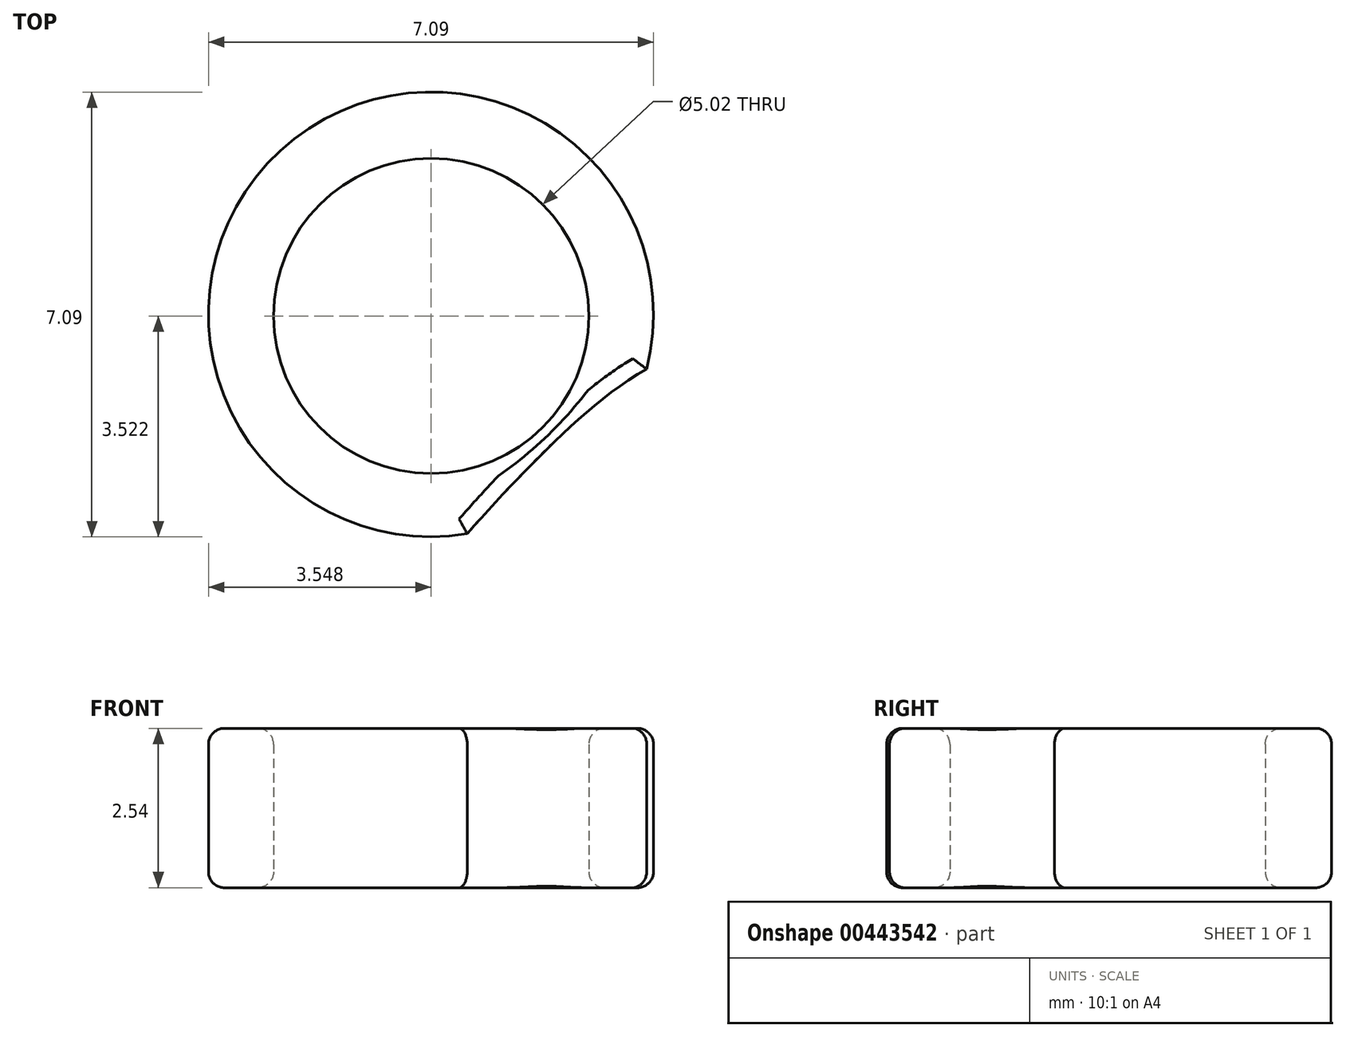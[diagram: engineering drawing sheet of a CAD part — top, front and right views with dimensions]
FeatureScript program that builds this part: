
annotation { "Feature Type Name" : "Feature", "Feature Type Description" : "" }
export const myFeature = defineFeature(function(context is Context, id is Id, definition is map)
    precondition{}
    {
        {
            var Q0;
            Q0=qCreatedBy(makeId("Top.planeOp"),FACE);
            var sketch = newSketch(context, id + "F0", { "sketchPlane" : qUnion([Q0])});
            skPoint(sketch, "E0.middle", {"position": v(0, 0) * mm});
            skFitSpline(sketch, "E1", {"points": [v(4.9, 17.87) * mm, v(1.19, 13.9) * mm, v(-0.75, 10.51) * mm, v(-1.88, 7.28) * mm, v(-2.45, 4.3) * mm, v(-2.45, 2.67) * mm, v(-2.45, 1.7) * mm, v(-2.53, 1.67) * mm, v(-2.84, 1.9) * mm, v(-3.8, 2.6) * mm, v(-6.06, 3.65) * mm, v(-8.48, 4.46) * mm, v(-10.99, 4.94) * mm, v(-12.12, 5.02) * mm, v(-12.52, 5.19) * mm, v(-13.9, 5.83) * mm, v(-15.51, 6.72) * mm, v(-17.05, 7.45) * mm, v(-17.7, 7.7) * mm, v(-18.2, 7.68) * mm, v(-18.43, 7.5) * mm, v(-18.4, 7.12) * mm, v(-18.06, 6.75) * mm, v(-17.5, 6.42) * mm, v(-15.46, 4.52) * mm, v(-13.92, 2.7) * mm, v(-12.57, 0.87) * mm, v(-11.56, -0.71) * mm, v(-10.31, -2.54) * mm, v(-8.68, -4.65) * mm, v(-7.29, -6.28) * mm, v(-5.5, -7.74) * mm, v(-4.25, -8.58) * mm, v(-3.82, -8.8) * mm, v(-3.8, -8.88) * mm, v(-3.94, -8.97) * mm, v(-4.5, -9.48) * mm, v(-5.62, -10.4) * mm, v(-6.9, -11.54) * mm, v(-8.08, -12.6) * mm, v(-9.05, -13.45) * mm, v(-10.59, -15) * mm, v(-12.5, -16.77) * mm, v(-13.39, -17.72) * mm, v(-14.07, -18.53) * mm, v(-14.26, -18.9) * mm, v(-14.13, -19.15) * mm, v(-13.45, -19.43) * mm, v(-12.08, -19.15) * mm, v(-10.64, -18.96) * mm, v(-8.34, -18.34) * mm, v(-5.72, -17.1) * mm, v(-4.04, -16.16) * mm, v(-3.78, -15.63) * mm, v(-3.6, -14.92) * mm, v(-3.5, -14.52) * mm, v(-3, -14.03) * mm, v(-2.52, -13.83) * mm, v(-1.83, -13.7) * mm, v(-0.65, -13.58) * mm, v(0.66, -13.52) * mm, v(2.71, -13.52) * mm, v(4.7, -13.33) * mm, v(7.58, -12.77) * mm, v(10.07, -11.53) * mm, v(12, -9.72) * mm, v(13.25, -7.54) * mm, v(13.72, -6.26) * mm, v(13.97, -5.64) * mm, v(14.1, -5.4) * mm, v(14.6, -5.14) * mm, v(15.52, -4.33) * mm, v(16.65, -3.09) * mm, v(17.33, -2.21) * mm, v(17.77, -1.78) * mm, v(18.52, -1.4) * mm, v(18.57, -1.27) * mm, v(18.53, -0.96) * mm, v(18.27, -0.63) * mm, v(18, -0.47) * mm, v(17.65, -0.47) * mm, v(17.32, -0.5) * mm, v(17.01, -0.5) * mm, v(16.64, -0.52) * mm, v(16.46, -0.4) * mm, v(16.22, -0.1) * mm, v(15.7, 0.4) * mm, v(14.6, 0.93) * mm, v(13.53, 1.12) * mm, v(12.62, 1.12) * mm, v(11.42, 0.74) * mm, v(10.56, 0.26) * mm, v(9.79, -0.32) * mm, v(9.16, -0.8) * mm, v(8.44, -1.42) * mm, v(8.15, -1.9) * mm, v(8.1, -1.88) * mm, v(8.09, -1.7) * mm, v(7.95, -1.02) * mm, v(7.84, -0.2) * mm, v(7.95, 0.28) * mm, v(8.27, 1.4) * mm, v(8.9, 2.7) * mm, v(9.52, 4.08) * mm, v(9.9, 5.33) * mm, v(9.95, 6.88) * mm, v(9.83, 8.57) * mm, v(9.45, 11.3) * mm, v(9.14, 13.24) * mm, v(8.58, 16.39) * mm, v(7.85, 18.57) * mm, v(7.29, 19.43) * mm, v(7.05, 19.43) * mm, v(6.96, 19.43) * mm, v(6.16, 18.65) * mm, v(4.9, 17.87) * mm]});
            skPoint(sketch, "E2.8.internal.snap0", {"position": v(21.12, -11.02) * mm});
            skPoint(sketch, "E2.0.internal.orphan", {"position": v(7.58, -10.64) * mm});
            skPoint(sketch, "E2.8.internal.orphan", {"position": v(7.24, -11.02) * mm});
            skPoint(sketch, "E3.78.internal.orphan", {"position": v(9.95, -9.77) * mm});
            skPoint(sketch, "E3.79.internal.orphan", {"position": v(10.07, -9.78) * mm});
            skPoint(sketch, "E3.88.internal.orphan", {"position": v(10.62, -9.72) * mm});
            skArc(sketch, "E4.trimOffspring", {"start": v(5.36, 18.16) * mm, "mid": v(-0.48, 21.64) * mm, "end": v(2.5, 15.53) * mm});
            skCircle(sketch, "E5", {"center": v(1.93, 19) * mm, "radius": 2.51 * mm});
            skSolve(sketch);
        }
        {
            var Q0;
            {var subQ0=sQuery(id+"F0.wireOp",EDGE,"E4.trimOffspring");Q0=makeQuery(id+"F0.imprint","IMPRINT",FACE,{"disambiguationData":[TD([[makeQuery(id+"F0.imprint","IMPRINT",EDGE,{"derivedFrom":subQ0}),1.0]])]});}
            extrude(context, id + "F1", {"entities" : qUnion([Q0]), "depth" : 2.54 * mm});
        }
        {
            var Q0;
            Q0=makeQuery(id+"F1.opExtrude","CAP_FACE",FACE,{"disambiguationData":[OSD([sQuery(id+"F0.wireOp",EDGE,"E1"),sQuery(id+"F0.wireOp",EDGE,"E4.trimOffspring"),sQuery(id+"F0.wireOp",EDGE,"E5")])],"isStart":false});
            var Q1;
            Q1=makeQuery(id+"F1.opExtrude","CAP_FACE",FACE,{"disambiguationData":[OSD([sQuery(id+"F0.wireOp",EDGE,"E1"),sQuery(id+"F0.wireOp",EDGE,"E4.trimOffspring"),sQuery(id+"F0.wireOp",EDGE,"E5")])],"isStart":true});
            fillet(context, id + "F2", {"entities" : qUnion([Q0, Q1]), "radius" : 0.25 * mm, "tangentPropagation" : true, "allowEdgeOverflow" : false});
        }
    });
